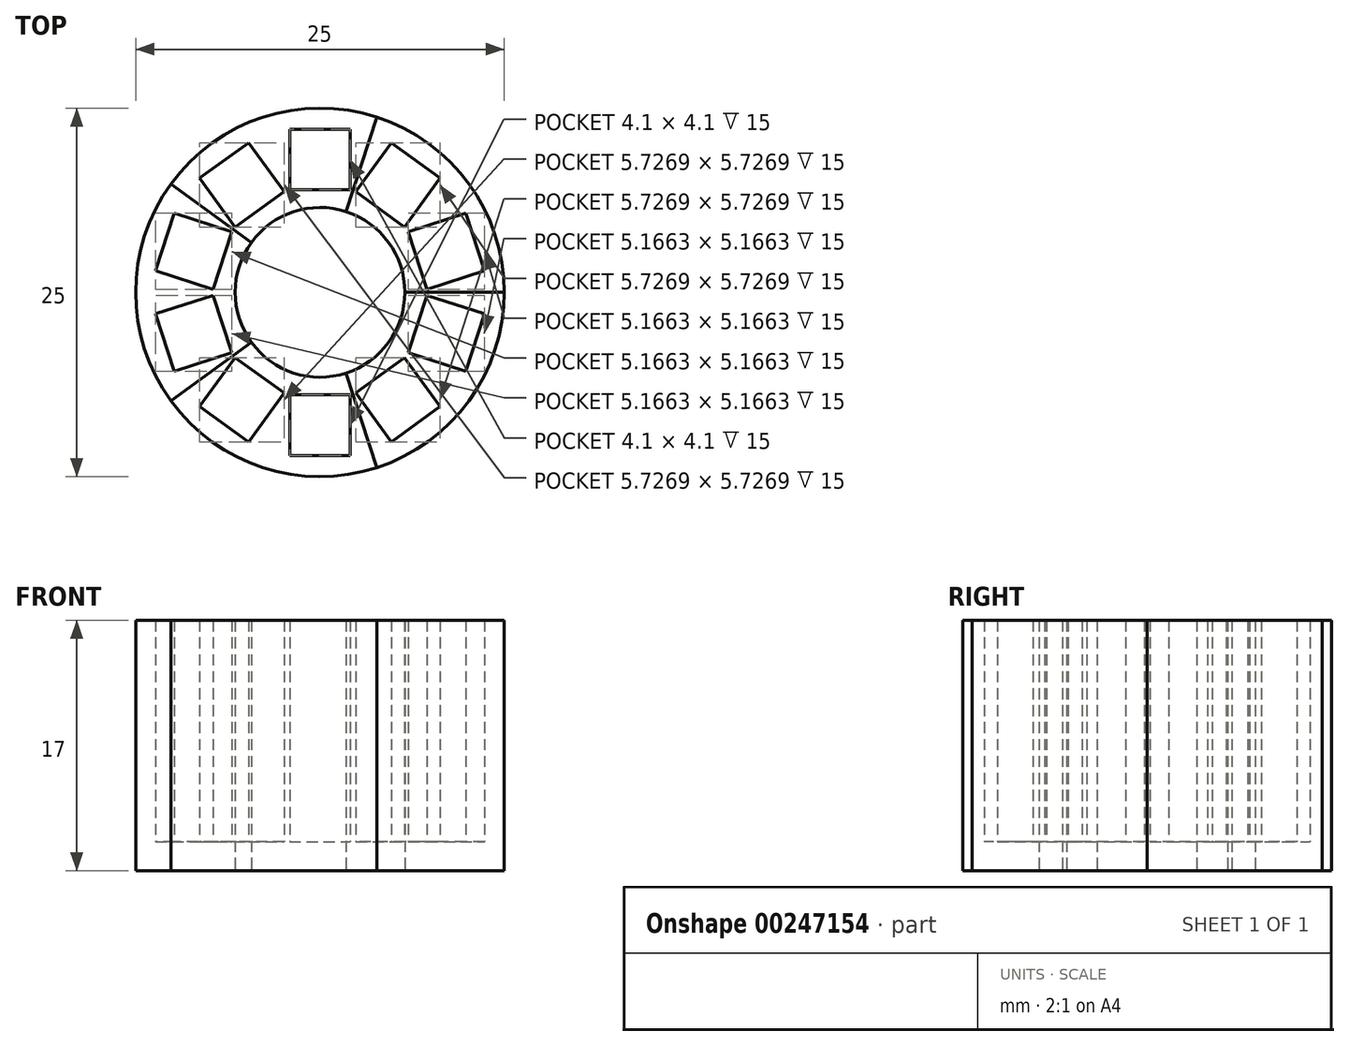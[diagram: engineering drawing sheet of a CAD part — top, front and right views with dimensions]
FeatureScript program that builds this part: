
annotation { "Feature Type Name" : "Feature", "Feature Type Description" : "" }
export const myFeature = defineFeature(function(context is Context, id is Id, definition is map)
    precondition{}
    {
        {
            var Q0;
            Q0=qCreatedBy(makeId("Top.planeOp"),FACE);
            var sketch = newSketch(context, id + "F0", { "sketchPlane" : qUnion([Q0])});
            skCircle(sketch, "E0", {"center": v(0, 0) * mm, "radius": 7.25 * mm});
            skLineSegment(sketch, "E1", {"start": v(0, 0) * mm, "end": v(-12.5, 0) * mm});
            skLineSegment(sketch, "E2", {"start": v(-12.5, 0) * mm, "end": v(0, 0) * mm});
            skLineSegment(sketch, "E3", {"start": v(0, 0) * mm, "end": v(-10.11, 7.35) * mm});
            skLineSegment(sketch, "E4", {"start": v(-7.25, 0.2) * mm, "end": v(-5.98, 4.1) * mm});
            skLineSegment(sketch, "E5", {"start": v(-5.98, 4.1) * mm, "end": v(-9.88, 5.37) * mm});
            skLineSegment(sketch, "E6", {"start": v(-9.88, 5.37) * mm, "end": v(-11.15, 1.47) * mm});
            skLineSegment(sketch, "E7", {"start": v(-11.15, 1.47) * mm, "end": v(-7.25, 0.2) * mm});
            skCircle(sketch, "E8", {"center": v(0, 0) * mm, "radius": 12.5 * mm});
            skCircle(sketch, "E9", {"center": v(0, 0) * mm, "radius": 5.76 * mm});
            skSolve(sketch);
        }
        {
            var Q0;
            {var subQ10=sQuery(id+"F0.wireOp",EDGE,"E5");Q0=makeQuery(id+"F0.imprint","IMPRINT",FACE,{"disambiguationData":[TD([[makeQuery(id+"F0.imprint","IMPRINT",EDGE,{"derivedFrom":subQ10}),-1.0]])]});}
            var Q1;
            {var subQ5=sQuery(id+"F0.wireOp",EDGE,"E4");Q1=makeQuery(id+"F0.imprint","IMPRINT",FACE,{"disambiguationData":[TD([[makeQuery(id+"F0.imprint","IMPRINT",EDGE,{"derivedFrom":subQ5}),-1.0]])]});}
            extrude(context, id + "F1", {"entities" : qUnion([Q0, Q1]), "depth" : 17 * mm, "offsetDistance" : 25 * mm});
        }
        {
            var Q0;
            {var subQ3=sQuery(id+"F0.wireOp",EDGE,"E5");Q0=makeQuery(id+"F0.imprint","IMPRINT",FACE,{"disambiguationData":[TD([[makeQuery(id+"F0.imprint","IMPRINT",EDGE,{"derivedFrom":subQ3}),1.0]])]});}
            var Q1;
            {var subQ0=sQuery(id+"F0.wireOp",EDGE,"E4");Q1=makeQuery(id+"F0.imprint","IMPRINT",FACE,{"disambiguationData":[TD([[makeQuery(id+"F0.imprint","IMPRINT",EDGE,{"derivedFrom":subQ0}),1.0]])]});}
            extrude(context, id + "F2", {"entities" : qUnion([Q0, Q1]), "operationType" : NewBodyOperationType.ADD, "depth" : 2 * mm, "offsetDistance" : 25 * mm});
        }
        {
            var Q0;
            Q0=makeQuery(id+"F1.opExtrude","SWEPT_BODY",BODY,{"disambiguationData":[OSD([sQuery(id+"F0.wireOp",EDGE,"E2"),sQuery(id+"F0.wireOp",EDGE,"E3"),sQuery(id+"F0.wireOp",EDGE,"E4"),sQuery(id+"F0.wireOp",EDGE,"E5"),sQuery(id+"F0.wireOp",EDGE,"E6"),sQuery(id+"F0.wireOp",EDGE,"E7"),sQuery(id+"F0.wireOp",EDGE,"E8"),sQuery(id+"F0.wireOp",EDGE,"E9")])]});
            var Q1;
            Q1=qCreatedBy(makeId("Front.planeOp"),FACE);
            mirror(context, id + "F3", {"operationType" : NewBodyOperationType.ADD, "entities" : qUnion([Q0]), "mirrorPlane" : qUnion([Q1])});
        }
        {
            var Q0;
            Q0=makeQuery(id+"F1.opExtrude","SWEPT_BODY",BODY,{"disambiguationData":[OSD([sQuery(id+"F0.wireOp",EDGE,"E2"),sQuery(id+"F0.wireOp",EDGE,"E3"),sQuery(id+"F0.wireOp",EDGE,"E4"),sQuery(id+"F0.wireOp",EDGE,"E5"),sQuery(id+"F0.wireOp",EDGE,"E6"),sQuery(id+"F0.wireOp",EDGE,"E7"),sQuery(id+"F0.wireOp",EDGE,"E8"),sQuery(id+"F0.wireOp",EDGE,"E9")])]});
            var Q1;
            Q1=makeQuery(id+"F3.opPattern","COPY",FACE,{"derivedFrom":makeQuery(id+"F1.opExtrude","SWEPT_FACE",FACE,{"disambiguationData":[OSD([sQuery(id+"F0.wireOp",EDGE,"E3")])]}),"instanceName":"1"});
            mirror(context, id + "F4", {"entities" : qUnion([Q0]), "mirrorPlane" : qUnion([Q1])});
        }
        {
            var Q0;
            Q0=makeQuery(id+"F4.opPattern","COPY",BODY,{"derivedFrom":makeQuery(id+"F1.opExtrude","SWEPT_BODY",BODY,{"disambiguationData":[OSD([sQuery(id+"F0.wireOp",EDGE,"E2"),sQuery(id+"F0.wireOp",EDGE,"E3"),sQuery(id+"F0.wireOp",EDGE,"E4"),sQuery(id+"F0.wireOp",EDGE,"E5"),sQuery(id+"F0.wireOp",EDGE,"E6"),sQuery(id+"F0.wireOp",EDGE,"E7"),sQuery(id+"F0.wireOp",EDGE,"E8"),sQuery(id+"F0.wireOp",EDGE,"E9")])]}),"instanceName":"1"});
            var Q1;
            Q1=makeQuery(id+"F4.opPattern","COPY",FACE,{"derivedFrom":makeQuery(id+"F1.opExtrude","SWEPT_FACE",FACE,{"disambiguationData":[OSD([sQuery(id+"F0.wireOp",EDGE,"E3")])]}),"instanceName":"1"});
            mirror(context, id + "F5", {"entities" : qUnion([Q0]), "mirrorPlane" : qUnion([Q1])});
        }
        {
            var Q0;
            Q0=makeQuery(id+"F5.opPattern","COPY",BODY,{"derivedFrom":makeQuery(id+"F4.opPattern","COPY",BODY,{"derivedFrom":makeQuery(id+"F1.opExtrude","SWEPT_BODY",BODY,{"disambiguationData":[OSD([sQuery(id+"F0.wireOp",EDGE,"E2"),sQuery(id+"F0.wireOp",EDGE,"E3"),sQuery(id+"F0.wireOp",EDGE,"E4"),sQuery(id+"F0.wireOp",EDGE,"E5"),sQuery(id+"F0.wireOp",EDGE,"E6"),sQuery(id+"F0.wireOp",EDGE,"E7"),sQuery(id+"F0.wireOp",EDGE,"E8"),sQuery(id+"F0.wireOp",EDGE,"E9")])]}),"instanceName":"1"}),"instanceName":"1"});
            var Q1;
            Q1=makeQuery(id+"F5.opPattern","COPY",FACE,{"derivedFrom":makeQuery(id+"F4.opPattern","COPY",FACE,{"derivedFrom":makeQuery(id+"F3.opPattern","COPY",FACE,{"derivedFrom":makeQuery(id+"F1.opExtrude","SWEPT_FACE",FACE,{"disambiguationData":[OSD([sQuery(id+"F0.wireOp",EDGE,"E3")])]}),"instanceName":"1"}),"instanceName":"1"}),"instanceName":"1"});
            mirror(context, id + "F6", {"entities" : qUnion([Q0]), "mirrorPlane" : qUnion([Q1])});
        }
        {
            var Q0;
            Q0=makeQuery(id+"F6.opPattern","COPY",BODY,{"derivedFrom":makeQuery(id+"F5.opPattern","COPY",BODY,{"derivedFrom":makeQuery(id+"F4.opPattern","COPY",BODY,{"derivedFrom":makeQuery(id+"F1.opExtrude","SWEPT_BODY",BODY,{"disambiguationData":[OSD([sQuery(id+"F0.wireOp",EDGE,"E2"),sQuery(id+"F0.wireOp",EDGE,"E3"),sQuery(id+"F0.wireOp",EDGE,"E4"),sQuery(id+"F0.wireOp",EDGE,"E5"),sQuery(id+"F0.wireOp",EDGE,"E6"),sQuery(id+"F0.wireOp",EDGE,"E7"),sQuery(id+"F0.wireOp",EDGE,"E8"),sQuery(id+"F0.wireOp",EDGE,"E9")])]}),"instanceName":"1"}),"instanceName":"1"}),"instanceName":"1"});
            var Q1;
            Q1=makeQuery(id+"F6.opPattern","COPY",FACE,{"derivedFrom":makeQuery(id+"F5.opPattern","COPY",FACE,{"derivedFrom":makeQuery(id+"F4.opPattern","COPY",FACE,{"derivedFrom":makeQuery(id+"F1.opExtrude","SWEPT_FACE",FACE,{"disambiguationData":[OSD([sQuery(id+"F0.wireOp",EDGE,"E3")])]}),"instanceName":"1"}),"instanceName":"1"}),"instanceName":"1"});
            mirror(context, id + "F7", {"entities" : qUnion([Q0]), "mirrorPlane" : qUnion([Q1])});
        }
    });
